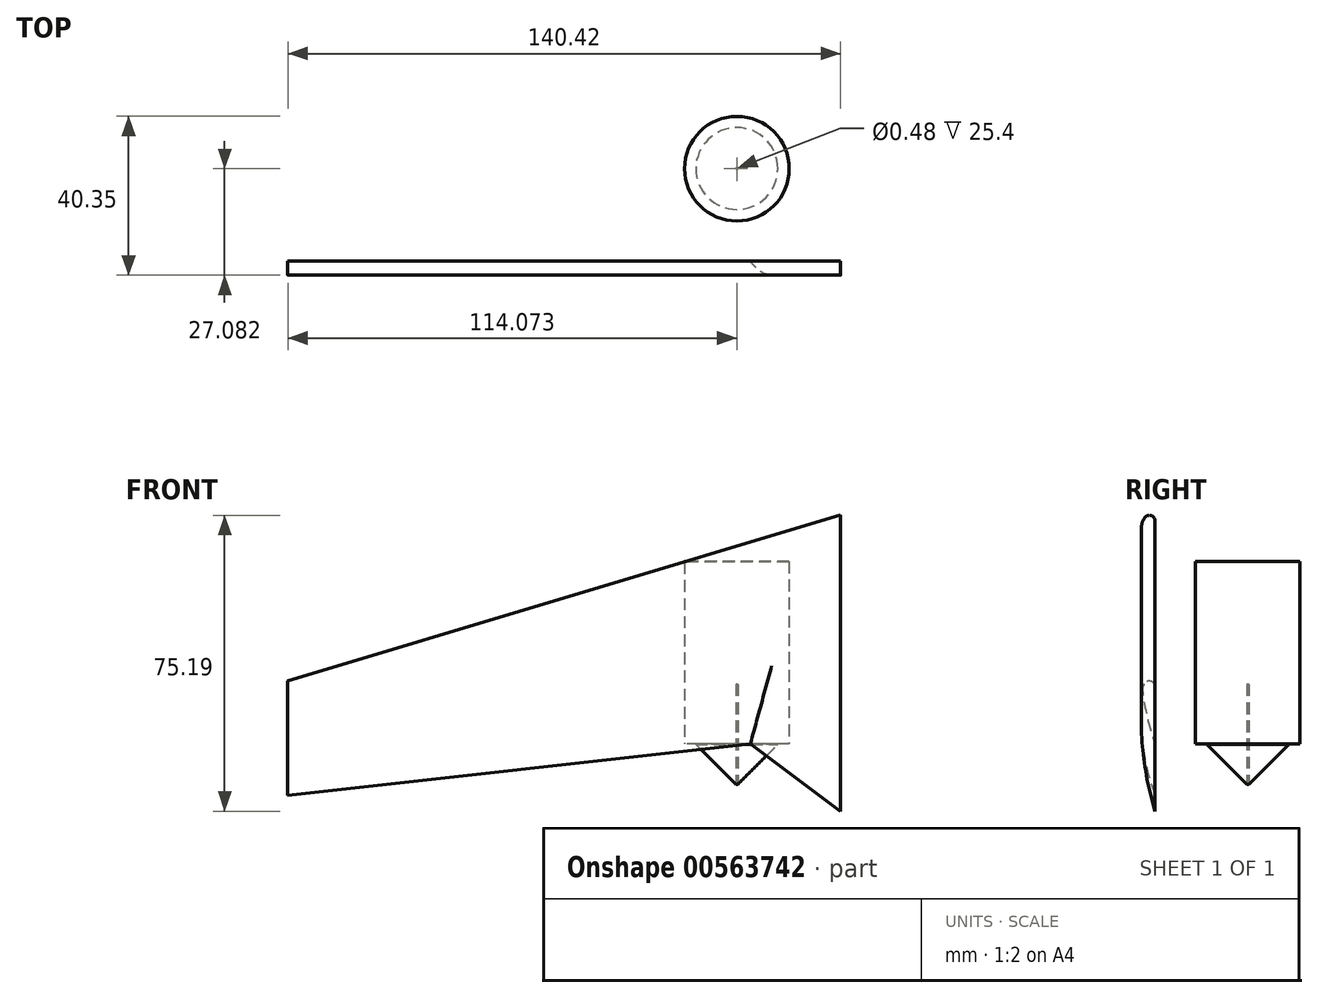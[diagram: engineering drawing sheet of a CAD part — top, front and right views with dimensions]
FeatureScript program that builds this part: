
annotation { "Feature Type Name" : "Feature", "Feature Type Description" : "" }
export const myFeature = defineFeature(function(context is Context, id is Id, definition is map)
    precondition{}
    {
        {
            var Q0;
            Q0=qCreatedBy(makeId("Front.planeOp"),FACE);
            var sketch = newSketch(context, id + "F0", { "sketchPlane" : qUnion([Q0])});
            skLineSegment(sketch, "E0", {"start": v(-76.16, 17.4) * mm, "end": v(-76.16, -13.13) * mm});
            skLineSegment(sketch, "E1", {"start": v(-76.16, 17.4) * mm, "end": v(64.26, 59.53) * mm});
            skLineSegment(sketch, "E2", {"start": v(-76.16, -13.13) * mm, "end": v(41.36, 0) * mm});
            skLineSegment(sketch, "E3", {"start": v(41.36, 0) * mm, "end": v(64.26, -17.1) * mm});
            skLineSegment(sketch, "E4", {"start": v(64.26, 59.53) * mm, "end": v(64.26, -17.1) * mm});
            skLineSegment(sketch, "E5", {"start": v(-76.16, 2.14) * mm, "end": v(-76.16, 17.4) * mm});
            skLineSegment(sketch, "E6", {"start": v(-76.16, -13.13) * mm, "end": v(-76.16, 2.14) * mm});
            skSolve(sketch);
        }
        {
            var Q0;
            Q0 = qSketchRegion(id + "F0", true);
            extrude(context, id + "F1", {"entities" : qUnion([Q0]), "depth" : 5.6 * mm, "offsetDistance" : 25.4 * mm});
        }
        {
            var Q0;
            Q0=makeQuery(id+"F1.opExtrude","CAP_EDGE",EDGE,{"disambiguationData":[OSD([sQuery(id+"F0.wireOp",EDGE,"E1")])],"isStart":false});
            var Q1;
            Q1=makeQuery(id+"F1.opExtrude","SWEPT_EDGE",EDGE,{"disambiguationData":[OSD([sQuery(id+"F0.wireOp",EDGE,"E2"),sQuery(id+"F0.wireOp",EDGE,"E6")])]});
            fillet(context, id + "F2", {"entities" : qUnion([Q0, Q1]), "radius" : 5.08 * mm, "tangentPropagation" : true, "allowEdgeOverflow" : false});
        }
        {
            var Q0;
            Q0=makeQuery(id+"F1.opExtrude","SWEPT_FACE",FACE,{"disambiguationData":[OSD([sQuery(id+"F0.wireOp",EDGE,"E1")])]});
            extrude(context, id + "F3", {"entities" : qUnion([Q0]), "operationType" : NewBodyOperationType.ADD, "depth" : 50.8 * mm, "offsetDistance" : 25.4 * mm});
        }
        {
            var Q0;
            Q0=makeQuery(id+"F1.opExtrude","SWEPT_BODY",BODY,{"disambiguationData":[OSD([sQuery(id+"F0.wireOp",EDGE,"E1"),sQuery(id+"F0.wireOp",EDGE,"E2"),sQuery(id+"F0.wireOp",EDGE,"E3"),sQuery(id+"F0.wireOp",EDGE,"E4"),sQuery(id+"F0.wireOp",EDGE,"E5"),sQuery(id+"F0.wireOp",EDGE,"E6")])]});
            deleteBodies(context, id + "F4", {"entities" : qUnion([Q0])});
        }
        {
            var Q0;
            Q0=makeQuery(id+"F0.imprint","IMPRINT",FACE,{"disambiguationData":[TD([[makeQuery(id+"F0.imprint","IMPRINT",EDGE,{"derivedFrom":sQuery(id+"F0.wireOp",EDGE,"E1")}),-1.0]])]});
            extrude(context, id + "F5", {"entities" : qUnion([Q0]), "depth" : 3.56 * mm, "offsetDistance" : 25.4 * mm});
        }
        {
            var Q0;
            Q0=makeQuery(id+"F5.opExtrude","CAP_EDGE",EDGE,{"disambiguationData":[OSD([sQuery(id+"F0.wireOp",EDGE,"E1")])],"isStart":false});
            fillet(context, id + "F6", {"entities" : qUnion([Q0]), "radius" : 5.08 * mm, "tangentPropagation" : true, "allowEdgeOverflow" : false});
        }
        {
            var Q0;
            Q0=makeQuery(id+"F5.opExtrude","CAP_EDGE",EDGE,{"disambiguationData":[OSD([sQuery(id+"F0.wireOp",EDGE,"E2")])],"isStart":false});
            var Q1;
            Q1=makeQuery(id+"F5.opExtrude","CAP_EDGE",EDGE,{"disambiguationData":[OSD([sQuery(id+"F0.wireOp",EDGE,"E3")])],"isStart":false});
            fillet(context, id + "F7", {"entities" : qUnion([Q0, Q1]), "radius" : 53.35 * mm, "tangentPropagation" : true, "allowEdgeOverflow" : false});
        }
        {
            var Q0;
            {var subQ0=sQuery(id+"F0.wireOp",EDGE,"E1");Q0=makeQuery(id+"F6.opFillet","BLEND_EDGE",EDGE,{"blendedFrom":[makeQuery(id+"F5.opExtrude","CAP_EDGE",EDGE,{"disambiguationData":[OSD([subQ0])],"isStart":false}),makeQuery(id+"F5.opExtrude","CAP_FACE",FACE,{"disambiguationData":[OSD([subQ0,sQuery(id+"F0.wireOp",EDGE,"E2"),sQuery(id+"F0.wireOp",EDGE,"E3"),sQuery(id+"F0.wireOp",EDGE,"E4"),sQuery(id+"F0.wireOp",EDGE,"E5"),sQuery(id+"F0.wireOp",EDGE,"E6")])],"isStart":true})],"blendedInto":[makeQuery(id+"F5.opExtrude","CAP_FACE",FACE,{"disambiguationData":[OSD([subQ0,sQuery(id+"F0.wireOp",EDGE,"E2"),sQuery(id+"F0.wireOp",EDGE,"E3"),sQuery(id+"F0.wireOp",EDGE,"E4"),sQuery(id+"F0.wireOp",EDGE,"E5"),sQuery(id+"F0.wireOp",EDGE,"E6")])],"isStart":true})]});}
            fillet(context, id + "F8", {"entities" : qUnion([Q0]), "radius" : 1.47 * mm, "tangentPropagation" : true, "allowEdgeOverflow" : false});
        }
        {
            var Q0;
            Q0=qCreatedBy(makeId("Top.planeOp"),FACE);
            var sketch = newSketch(context, id + "F9", { "sketchPlane" : qUnion([Q0])});
            skCircle(sketch, "E7", {"center": v(37.91, 23.49) * mm, "radius": 13.3 * mm});
            skSolve(sketch);
        }
        {
            var Q0;
            Q0=makeQuery(id+"F9.imprint","IMPRINT",FACE,{"disambiguationData":[TD([[makeQuery(id+"F9.imprint","IMPRINT",EDGE,{"derivedFrom":sQuery(id+"F9.wireOp",EDGE,"E7")}),1.0]])]});
            extrude(context, id + "F10", {"entities" : qUnion([Q0]), "depth" : 46.35 * mm, "offsetDistance" : 25.4 * mm});
        }
        {
            var Q0;
            Q0=qCreatedBy(makeId("Top.planeOp"),FACE);
            var sketch = newSketch(context, id + "F11", { "sketchPlane" : qUnion([Q0])});
            skCircle(sketch, "E8", {"center": v(37.91, 23.52) * mm, "radius": 10.4 * mm});
            skSolve(sketch);
        }
        {
            var Q0;
            Q0=makeQuery(id+"F11.imprint","IMPRINT",FACE,{"disambiguationData":[TD([[makeQuery(id+"F11.imprint","IMPRINT",EDGE,{"derivedFrom":sQuery(id+"F11.wireOp",EDGE,"E8")}),1.0]])]});
            extrude(context, id + "F12", {"entities" : qUnion([Q0]), "operationType" : NewBodyOperationType.ADD, "oppositeDirection" : true, "depth" : 16.7 * mm, "offsetDistance" : 25.4 * mm});
        }
        {
            var Q0;
            Q0=makeQuery(id+"F12.opExtrude","CAP_FACE",FACE,{"disambiguationData":[OSD([sQuery(id+"F11.wireOp",EDGE,"E8")])],"isStart":false});
            extrude(context, id + "F13", {"entities" : qUnion([Q0]), "operationType" : NewBodyOperationType.REMOVE, "oppositeDirection" : true, "depth" : 6.42 * mm, "offsetDistance" : 25.4 * mm});
        }
        {
            var Q0;
            Q0=makeQuery(id+"F13.boolean.opBoolean","COPY",FACE,{"derivedFrom":makeQuery(id+"F13.opExtrude","CAP_FACE",FACE,{"disambiguationData":[OSD([sQuery(id+"F11.wireOp",EDGE,"E8")])],"isStart":false})});
            chamfer(context, id + "F14", {"entities" : qUnion([Q0]), "width" : 10.16 * mm, "tangentPropagation" : true});
        }
        {
            var Q0;
            Q0=makeQuery(id+"F13.boolean.opBoolean","COPY",FACE,{"derivedFrom":makeQuery(id+"F13.opExtrude","CAP_FACE",FACE,{"disambiguationData":[OSD([sQuery(id+"F11.wireOp",EDGE,"E8")])],"isStart":false})});
            extrude(context, id + "F15", {"entities" : qUnion([Q0]), "operationType" : NewBodyOperationType.REMOVE, "oppositeDirection" : true, "depth" : 25.4 * mm, "offsetDistance" : 25.4 * mm});
        }
    });
